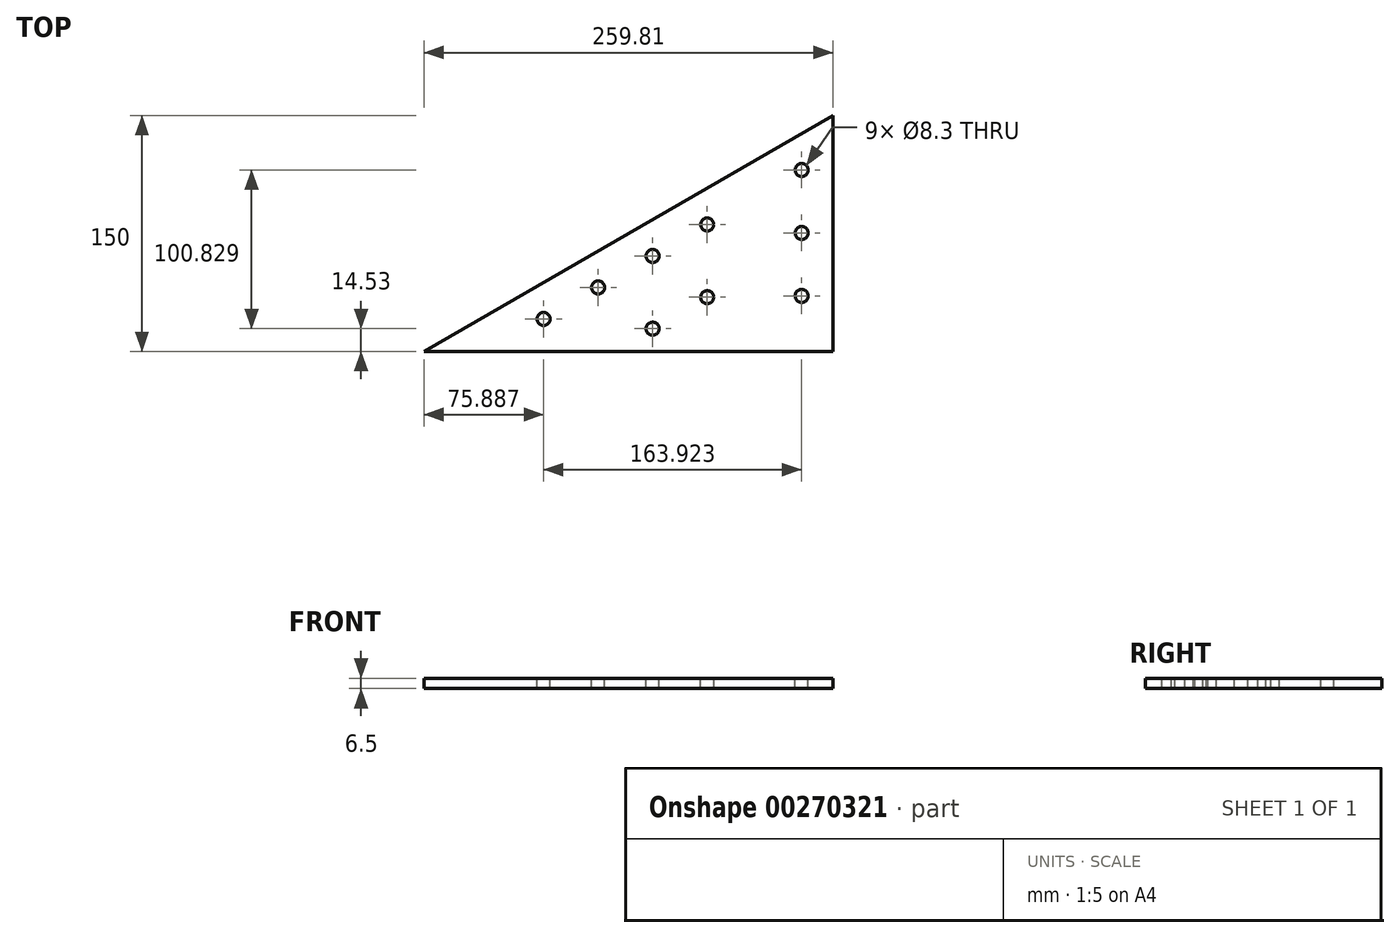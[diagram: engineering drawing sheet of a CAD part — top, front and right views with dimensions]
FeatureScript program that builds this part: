
annotation { "Feature Type Name" : "Feature", "Feature Type Description" : "" }
export const myFeature = defineFeature(function(context is Context, id is Id, definition is map)
    precondition{}
    {
        {
            var Q0;
            Q0=qCreatedBy(makeId("Top.planeOp"),FACE);
            var sketch = newSketch(context, id + "F0", { "sketchPlane" : qUnion([Q0])});
            skLineSegment(sketch, "E0", {"start": v(0, 0) * mm, "end": v(0, 150) * mm});
            skLineSegment(sketch, "E1", {"start": v(0, 150) * mm, "end": v(-259.8, 0) * mm});
            skLineSegment(sketch, "E2", {"start": v(-259.8, 0) * mm, "end": v(0, 0) * mm});
            skSolve(sketch);
        }
        {
            var Q0;
            Q0 = qSketchRegion(id + "F0", true);
            extrude(context, id + "F1", {"entities" : qUnion([Q0]), "depth" : 6.5 * mm});
        }
        {
            var Q0;
            Q0=makeQuery(id+"F1.opExtrude","CAP_FACE",FACE,{"disambiguationData":[OSD([sQuery(id+"F0.wireOp",EDGE,"E0"),sQuery(id+"F0.wireOp",EDGE,"E1"),sQuery(id+"F0.wireOp",EDGE,"E2")])],"isStart":false});
            var sketch = newSketch(context, id + "F2", { "sketchPlane" : qUnion([Q0])});
            skLineSegment(sketch, "E3.0", {"start": v(-20, 5) * mm, "end": v(-20, 180.71) * mm, "construction": true});
            skLineSegment(sketch, "E4.0", {"start": v(57.04, 159.84) * mm, "end": v(-271.3, -29.73) * mm, "construction": true});
            skLineSegment(sketch, "E5.0", {"start": v(-22.52, 67.72) * mm, "end": v(-194.69, -31.68) * mm, "construction": true});
            skPoint(sketch, "E6", {"position": v(-20, 115.36) * mm});
            skPoint(sketch, "E7", {"position": v(-20, 75.36) * mm});
            skPoint(sketch, "E8", {"position": v(-20, 35.36) * mm});
            skPoint(sketch, "E9", {"position": v(-149.28, 40.72) * mm});
            skPoint(sketch, "E10", {"position": v(-114.64, 60.72) * mm});
            skPoint(sketch, "E11", {"position": v(-80, 80.72) * mm});
            skPoint(sketch, "E12", {"position": v(-114.64, 14.53) * mm});
            skPoint(sketch, "E13", {"position": v(-80, 34.53) * mm});
            skPoint(sketch, "E14", {"position": v(-183.92, 20.72) * mm});
            skSolve(sketch);
        }
        {
            var Q0;
            Q0=sQuery(id+"F2.wireOp",VERTEX,"E11");
            var Q1;
            Q1=sQuery(id+"F2.wireOp",VERTEX,"E10");
            var Q2;
            Q2=sQuery(id+"F2.wireOp",VERTEX,"E13");
            var Q3;
            Q3=sQuery(id+"F2.wireOp",VERTEX,"E6");
            var Q4;
            Q4=sQuery(id+"F2.wireOp",VERTEX,"E7");
            var Q5;
            Q5=sQuery(id+"F2.wireOp",VERTEX,"E8");
            var Q6;
            Q6=sQuery(id+"F2.wireOp",VERTEX,"E12");
            var Q7;
            Q7=sQuery(id+"F2.wireOp",VERTEX,"E9");
            var Q8;
            Q8=sQuery(id+"F2.wireOp",VERTEX,"E14");
            var Q9;
            Q9=makeQuery(id+"F1.opExtrude","SWEPT_BODY",BODY,{"disambiguationData":[OSD([sQuery(id+"F0.wireOp",EDGE,"E0"),sQuery(id+"F0.wireOp",EDGE,"E1"),sQuery(id+"F0.wireOp",EDGE,"E2")])]});
            hole(context, id + "F3", {"style" : HoleStyle.SIMPLE, "endStyle" : HoleEndStyle.THROUGH, "standardTappedOrClearance" : lookupTablePath({ "standard" : "ISO", "size" : "8.3", "type" : "Drilled" }), "standardBlindInLast" : lookupTablePath({ "standard" : "ISO", "size" : "8.3", "type" : "Drilled" }), "holeDiameter" : 8.3 * mm, "tappedDepth" : 12 * mm, "tapClearance" : 3, "locations" : qUnion([Q0, Q1, Q2, Q3, Q4, Q5, Q6, Q7, Q8]), "scope" : qUnion([Q9])});
        }
    });
